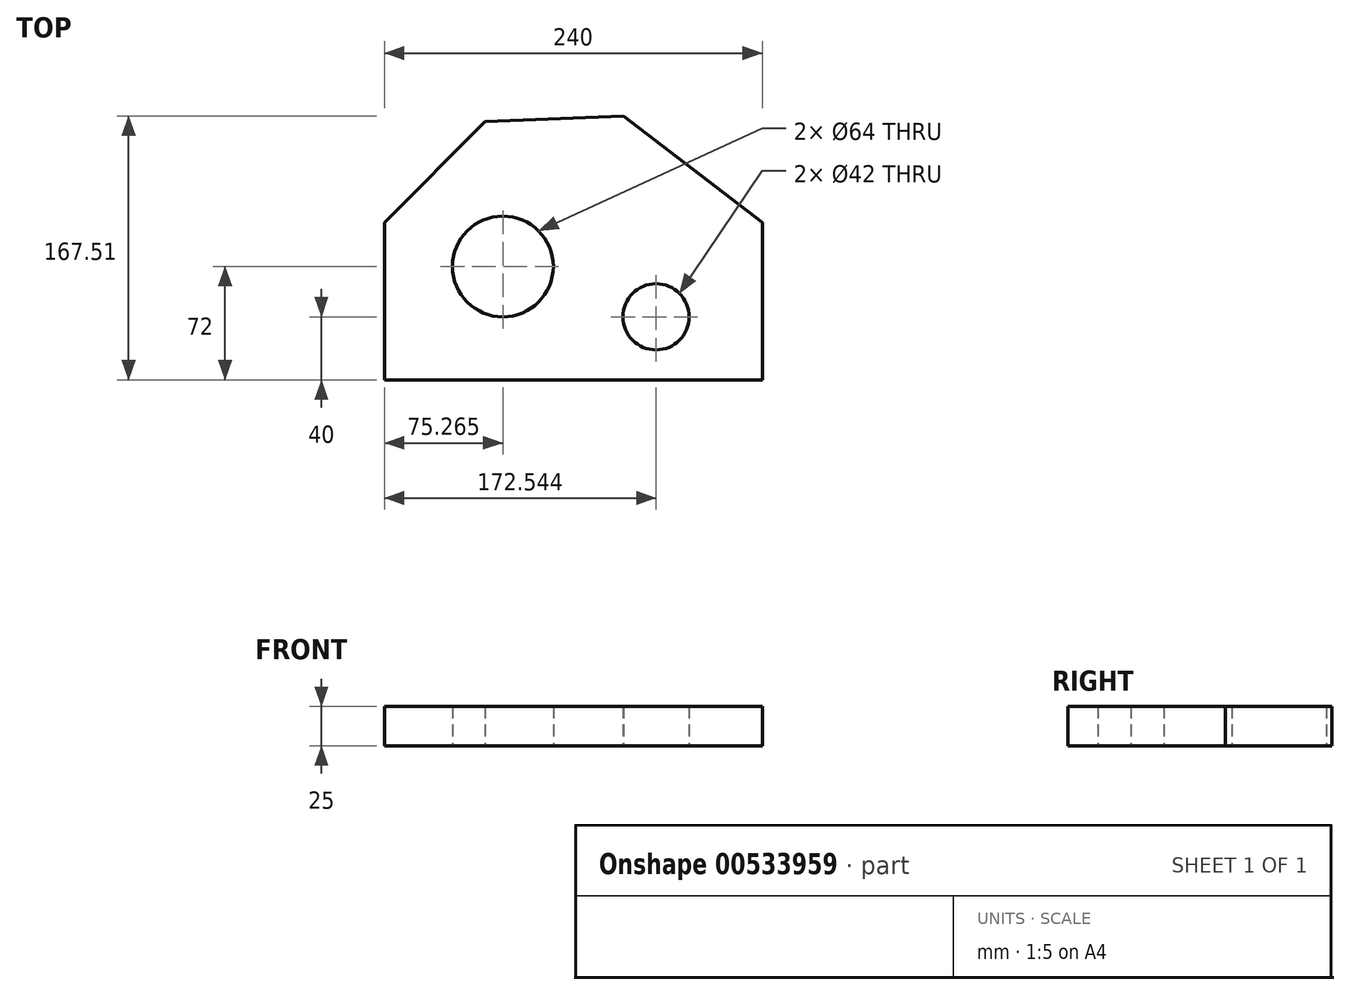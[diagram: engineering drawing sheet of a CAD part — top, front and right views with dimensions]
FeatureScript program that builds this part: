
annotation { "Feature Type Name" : "Feature", "Feature Type Description" : "" }
export const myFeature = defineFeature(function(context is Context, id is Id, definition is map)
    precondition{}
    {
        {
            var Q0;
            Q0=qCreatedBy(makeId("Top.planeOp"),FACE);
            var sketch = newSketch(context, id + "F0", { "sketchPlane" : qUnion([Q0])});
            skLineSegment(sketch, "E0", {"start": v(-119.71, 33.59) * mm, "end": v(-119.71, -66.41) * mm});
            skLineSegment(sketch, "E1", {"start": v(-119.71, -66.41) * mm, "end": v(120.29, -66.41) * mm});
            skLineSegment(sketch, "E2", {"start": v(120.29, -66.41) * mm, "end": v(120.29, 33.59) * mm});
            skLineSegment(sketch, "E3", {"start": v(120.29, 33.59) * mm, "end": v(32.22, 101.1) * mm});
            skLineSegment(sketch, "E4", {"start": v(32.22, 101.1) * mm, "end": v(-55.71, 97.59) * mm});
            skLineSegment(sketch, "E5", {"start": v(-119.71, 33.59) * mm, "end": v(-55.71, 97.59) * mm});
            skCircle(sketch, "E6", {"center": v(-44.44, 5.59) * mm, "radius": 32 * mm});
            skCircle(sketch, "E7", {"center": v(52.83, -26.41) * mm, "radius": 21 * mm});
            skSolve(sketch);
        }
        {
            var Q0;
            Q0 = qSketchRegion(id + "F0", true);
            extrude(context, id + "F1", {"entities" : qUnion([Q0]), "depth" : 25 * mm, "offsetDistance" : 25 * mm});
        }
    });
